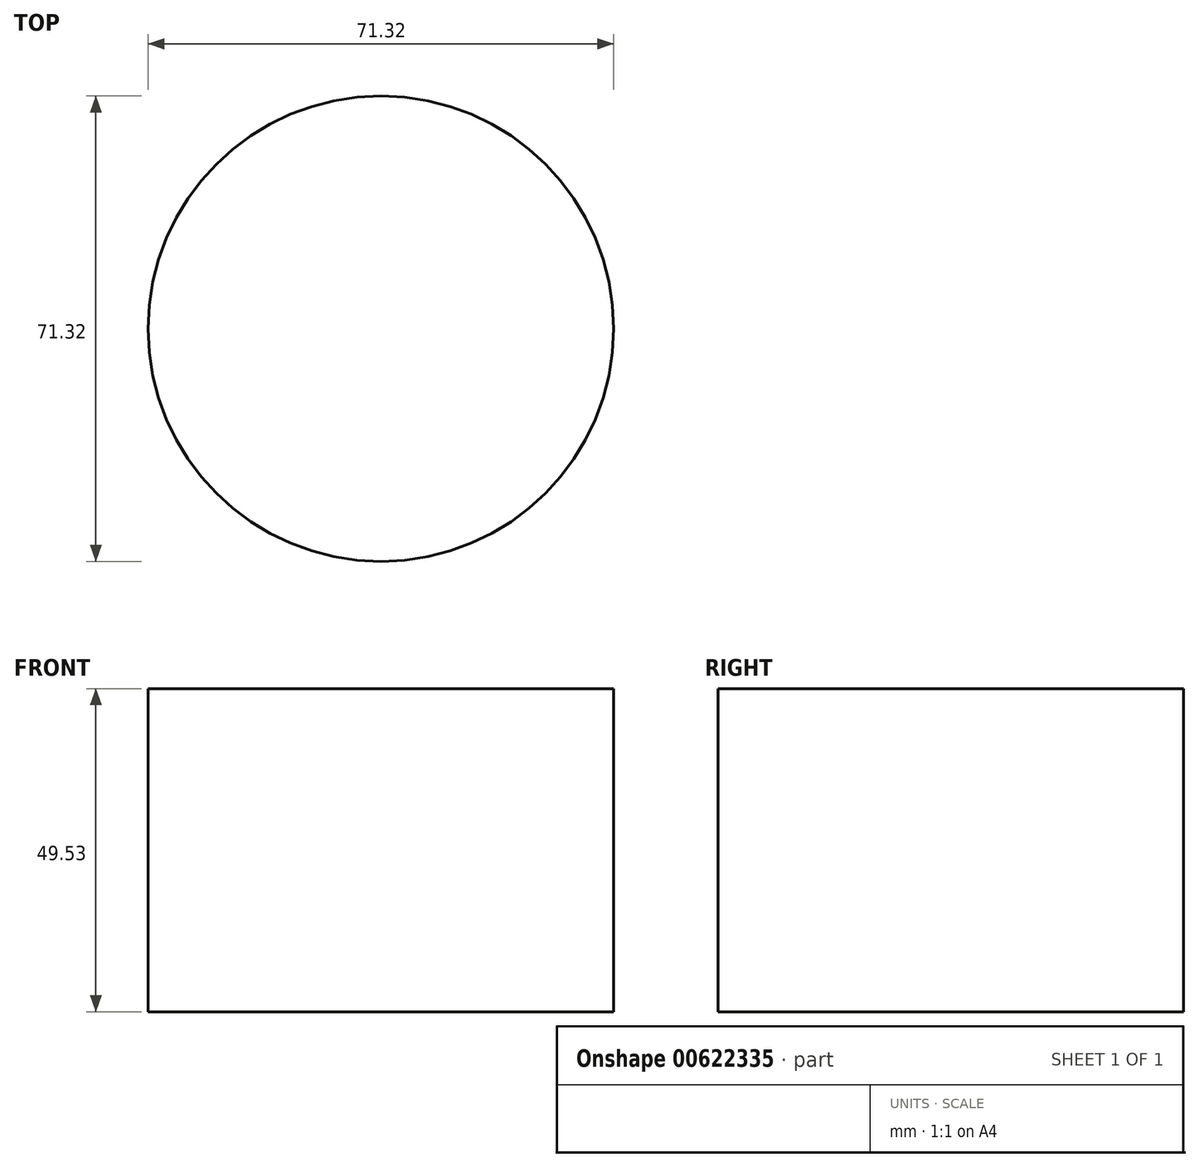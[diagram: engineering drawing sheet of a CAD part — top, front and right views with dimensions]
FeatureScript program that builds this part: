
annotation { "Feature Type Name" : "Feature", "Feature Type Description" : "" }
export const myFeature = defineFeature(function(context is Context, id is Id, definition is map)
    precondition{}
    {
        {
            var Q0;
            Q0=qCreatedBy(makeId("Top.planeOp"),FACE);
            var sketch = newSketch(context, id + "F0", { "sketchPlane" : qUnion([Q0])});
            skCircle(sketch, "E0", {"center": v(0, 0) * mm, "radius": 35.66 * mm});
            skSolve(sketch);
        }
        {
            var Q0;
            Q0=makeQuery(id+"F0.imprint","IMPRINT",FACE,{"disambiguationData":[TD([[makeQuery(id+"F0.imprint","IMPRINT",EDGE,{"derivedFrom":sQuery(id+"F0.wireOp",EDGE,"E0")}),1.0]])]});
            extrude(context, id + "F1", {"entities" : qUnion([Q0]), "oppositeDirection" : true, "depth" : 49.53 * mm, "offsetDistance" : 25.4 * mm});
        }
    });
